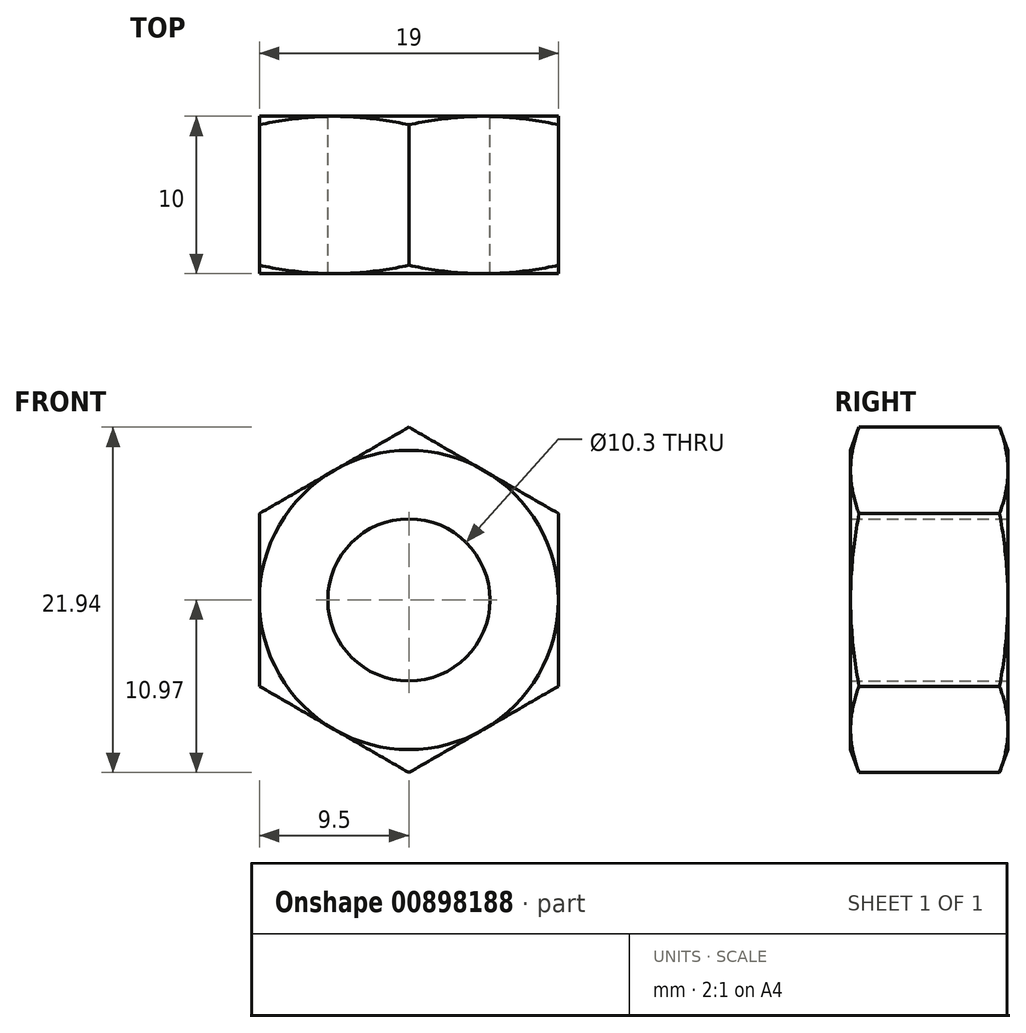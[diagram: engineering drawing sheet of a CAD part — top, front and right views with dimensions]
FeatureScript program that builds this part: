
annotation { "Feature Type Name" : "Feature", "Feature Type Description" : "" }
export const myFeature = defineFeature(function(context is Context, id is Id, definition is map)
    precondition{}
    {
        {
            var Q0;
            Q0=qCreatedBy(makeId("Front.planeOp"),FACE);
            var sketch = newSketch(context, id + "F0", { "sketchPlane" : qUnion([Q0])});
            skLineSegment(sketch, "E0", {"start": v(-9.5, 0) * mm, "end": v(9.5, 0) * mm, "construction": true});
            skCircle(sketch, "E1.cCircle", {"center": v(0, 0) * mm, "radius": 9.5 * mm});
            skLineSegment(sketch, "E1.0", {"start": v(9.5, 5.48) * mm, "end": v(9.5, -5.48) * mm});
            skLineSegment(sketch, "E1.1", {"start": v(9.5, -5.48) * mm, "end": v(0, -10.97) * mm});
            skLineSegment(sketch, "E1.2", {"start": v(0, -10.97) * mm, "end": v(-9.5, -5.48) * mm});
            skLineSegment(sketch, "E1.3", {"start": v(-9.5, -5.48) * mm, "end": v(-9.5, 5.48) * mm});
            skLineSegment(sketch, "E1.4", {"start": v(-9.5, 5.48) * mm, "end": v(0, 10.97) * mm});
            skLineSegment(sketch, "E1.5", {"start": v(0, 10.97) * mm, "end": v(9.5, 5.48) * mm});
            skPoint(sketch, "E1.0.midPoint", {"position": v(9.5, 0) * mm});
            skLineSegment(sketch, "E2", {"start": v(0, 10.97) * mm, "end": v(0, -10.97) * mm, "construction": true});
            skCircle(sketch, "E3", {"center": v(0, 0) * mm, "radius": 10.97 * mm});
            skSolve(sketch);
        }
        {
            var Q0;
            Q0=qCreatedBy(makeId("Right.planeOp"),FACE);
            var sketch = newSketch(context, id + "F1", { "sketchPlane" : qUnion([Q0])});
            skLineSegment(sketch, "E4.0", {"start": v(0, -9.5) * mm, "end": v(0, 9.5) * mm});
            skPoint(sketch, "E4.1", {"position": v(0, 10.97) * mm});
            skPoint(sketch, "E4.2", {"position": v(0, -10.97) * mm});
            skLineSegment(sketch, "E5.MirrorCS", {"start": v(-9.47, 10.97) * mm, "end": v(-10, 9.5) * mm});
            skLineSegment(sketch, "E6", {"start": v(-9.47, 10.97) * mm, "end": v(-0.53, 10.97) * mm});
            skLineSegment(sketch, "E7", {"start": v(-0.53, 10.97) * mm, "end": v(0, 9.5) * mm});
            skLineSegment(sketch, "E8", {"start": v(0, 9.5) * mm, "end": v(0, 0) * mm, "construction": true});
            skLineSegment(sketch, "E9", {"start": v(0, 0) * mm, "end": v(-10, 0) * mm});
            skLineSegment(sketch, "E10", {"start": v(-10, 9.5) * mm, "end": v(-10, 0) * mm});
            skSolve(sketch);
        }
        {
            var Q0;
            Q0=makeQuery(id+"F1.imprint","IMPRINT",FACE,{"disambiguationData":[TD([[makeQuery(id+"F1.imprint","IMPRINT",EDGE,{"derivedFrom":sQuery(id+"F1.wireOp",EDGE,"E5.MirrorCS")}),1.0]])]});
            var Q1;
            Q1=sQuery(id+"F1.wireOp",EDGE,"E9");
            revolve(context, id + "F2", {"surfaceOperationType" : NewSurfaceOperationType.NEW, "entities" : qUnion([Q0]), "axis" : qUnion([Q1]), "revolveType" : RevolveType.FULL});
        }
        {
            var Q0;
            {var subQ1=sQuery(id+"F0.wireOp",EDGE,"E1.4");var subQ3=makeQuery(id+"F0.imprint","INTERSECT",VERTEX,{"derivedFrom":[sQuery(id+"F0.wireOp",EDGE,"E1.cCircle"),subQ1]});Q0=makeQuery(id+"F0.imprint","IMPRINT",FACE,{"disambiguationData":[TD([[makeQuery(id+"F0.imprint","IMPRINT",EDGE,{"disambiguationData":[TD([[subQ3,1.0]])],"derivedFrom":subQ1}),1.0]])]});}
            var Q1;
            {var subQ1=sQuery(id+"F0.wireOp",EDGE,"E1.3");var subQ3=makeQuery(id+"F0.imprint","INTERSECT",VERTEX,{"derivedFrom":[sQuery(id+"F0.wireOp",EDGE,"E1.cCircle"),subQ1]});Q1=makeQuery(id+"F0.imprint","IMPRINT",FACE,{"disambiguationData":[TD([[makeQuery(id+"F0.imprint","IMPRINT",EDGE,{"disambiguationData":[TD([[subQ3,1.0]])],"derivedFrom":subQ1}),1.0]])]});}
            var Q2;
            {var subQ1=sQuery(id+"F0.wireOp",EDGE,"E1.5");var subQ3=makeQuery(id+"F0.imprint","INTERSECT",VERTEX,{"derivedFrom":[sQuery(id+"F0.wireOp",EDGE,"E1.cCircle"),subQ1]});Q2=makeQuery(id+"F0.imprint","IMPRINT",FACE,{"disambiguationData":[TD([[makeQuery(id+"F0.imprint","IMPRINT",EDGE,{"disambiguationData":[TD([[subQ3,1.0]])],"derivedFrom":subQ1}),1.0]])]});}
            var Q3;
            {var subQ1=sQuery(id+"F0.wireOp",EDGE,"E1.0");var subQ3=makeQuery(id+"F0.imprint","INTERSECT",VERTEX,{"derivedFrom":[sQuery(id+"F0.wireOp",EDGE,"E1.cCircle"),subQ1]});Q3=makeQuery(id+"F0.imprint","IMPRINT",FACE,{"disambiguationData":[TD([[makeQuery(id+"F0.imprint","IMPRINT",EDGE,{"disambiguationData":[TD([[subQ3,1.0]])],"derivedFrom":subQ1}),1.0]])]});}
            var Q4;
            {var subQ1=sQuery(id+"F0.wireOp",EDGE,"E1.1");var subQ3=makeQuery(id+"F0.imprint","INTERSECT",VERTEX,{"derivedFrom":[sQuery(id+"F0.wireOp",EDGE,"E1.cCircle"),subQ1]});Q4=makeQuery(id+"F0.imprint","IMPRINT",FACE,{"disambiguationData":[TD([[makeQuery(id+"F0.imprint","IMPRINT",EDGE,{"disambiguationData":[TD([[subQ3,1.0]])],"derivedFrom":subQ1}),1.0]])]});}
            var Q5;
            {var subQ1=sQuery(id+"F0.wireOp",EDGE,"E1.2");var subQ3=makeQuery(id+"F0.imprint","INTERSECT",VERTEX,{"derivedFrom":[sQuery(id+"F0.wireOp",EDGE,"E1.cCircle"),subQ1]});Q5=makeQuery(id+"F0.imprint","IMPRINT",FACE,{"disambiguationData":[TD([[makeQuery(id+"F0.imprint","IMPRINT",EDGE,{"disambiguationData":[TD([[subQ3,1.0]])],"derivedFrom":subQ1}),1.0]])]});}
            extrude(context, id + "F3", {"entities" : qUnion([Q0, Q1, Q2, Q3, Q4, Q5]), "operationType" : NewBodyOperationType.REMOVE, "endBound" : BoundingType.THROUGH_ALL, "oppositeDirection" : true, "depth" : 25 * mm, "offsetDistance" : 25 * mm, "hasSecondDirection" : true, "secondDirectionBound" : SecondDirectionBoundingType.THROUGH_ALL, "secondDirectionOppositeDirection" : false, "secondDirectionDepth" : 25 * mm});
        }
        {
            var Q0;
            Q0=sQuery(id+"F0.wireOp",VERTEX,"E1.cCircle.center");
            var Q1;
            Q1=makeQuery(id+"F2.opRevolve","SWEPT_BODY",BODY,{"disambiguationData":[OSD([sQuery(id+"F1.wireOp",EDGE,"q88OuVeV-Xssd-KdqV-jFtn-j9xKU6Sgstji"),sQuery(id+"F1.wireOp",EDGE,"m6PsllCo-agTw-A9O4-2Ydg-0b9s2DICKGsd"),sQuery(id+"F1.wireOp",EDGE,"BdBtqhzv-rrtv-71de-whUi-Sthj0NWjNpZN"),sQuery(id+"F1.wireOp",EDGE,"j5BlujB0-zh70-Cei2-xDxi-jKAxp30yvdPL"),sQuery(id+"F1.wireOp",EDGE,"5fe2b027-1bad-4d8e-b947-d590a72a6a090.MirrorCS"),sQuery(id+"F1.wireOp",EDGE,"5fe2b027-1bad-4d8e-b947-d590a72a6a091.MirrorCS"),sQuery(id+"F1.wireOp",EDGE,"E5.MirrorCS")])]});
            hole(context, id + "F4", {"style" : HoleStyle.SIMPLE, "endStyle" : HoleEndStyle.THROUGH, "oppositeDirection" : true, "standardTappedOrClearance" : lookupTablePath({ "standard" : "ISO", "engagement" : "75%", "pitch" : "1.75 mm", "size" : "M12", "type" : "Tapped" }), "standardBlindInLast" : lookupTablePath({ "standard" : "ISO", "engagement" : "75%", "pitch" : "1.75 mm", "size" : "M12", "type" : "Tapped" }), "holeDiameter" : 10.3 * mm, "majorDiameter" : 12 * mm, "showTappedDepth" : true, "tappedDepth" : 14 * mm, "tapClearance" : 3, "locations" : qUnion([Q0]), "scope" : qUnion([Q1])});
        }
    });
